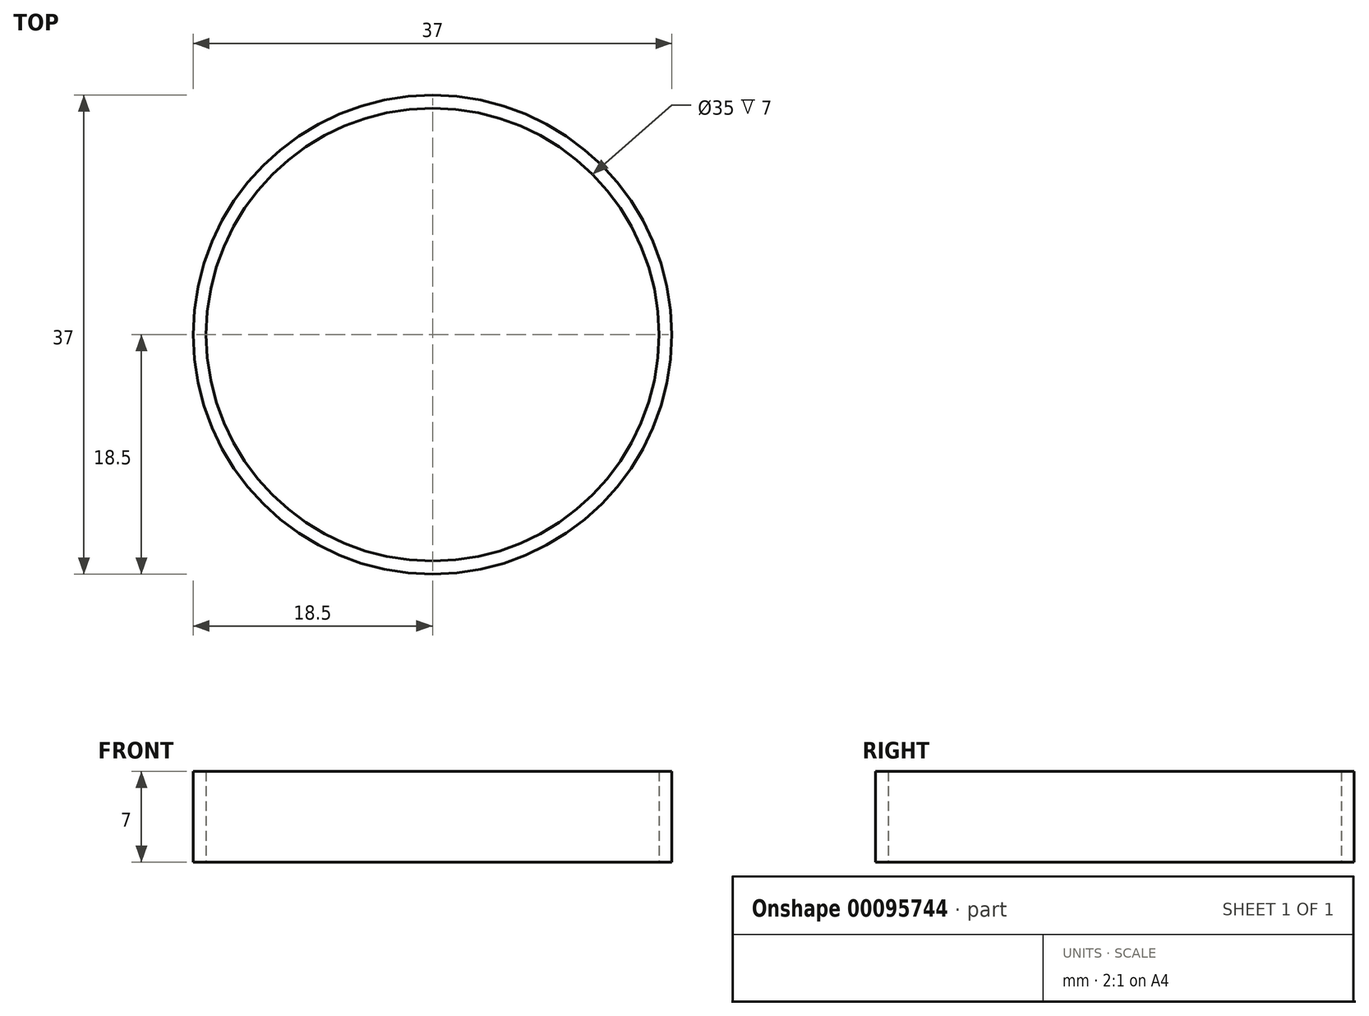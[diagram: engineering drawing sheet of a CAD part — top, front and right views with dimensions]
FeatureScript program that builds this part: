
annotation { "Feature Type Name" : "Feature", "Feature Type Description" : "" }
export const myFeature = defineFeature(function(context is Context, id is Id, definition is map)
    precondition{}
    {
        {
            var Q0;
            Q0=qCreatedBy(makeId("Top.planeOp"),FACE);
            var sketch = newSketch(context, id + "F0", { "sketchPlane" : qUnion([Q0])});
            skCircle(sketch, "E0", {"center": v(0, 0) * mm, "radius": 17.5 * mm});
            skCircle(sketch, "E1", {"center": v(0, 0) * mm, "radius": 18.5 * mm});
            skSolve(sketch);
        }
        {
            var Q0;
            Q0=makeQuery(id+"F0.imprint","IMPRINT",FACE,{"disambiguationData":[TD([[makeQuery(id+"F0.imprint","IMPRINT",EDGE,{"derivedFrom":sQuery(id+"F0.wireOp",EDGE,"E0")}),-1.0]])]});
            extrude(context, id + "F1", {"entities" : qUnion([Q0]), "depth" : 7 * mm});
        }
    });
